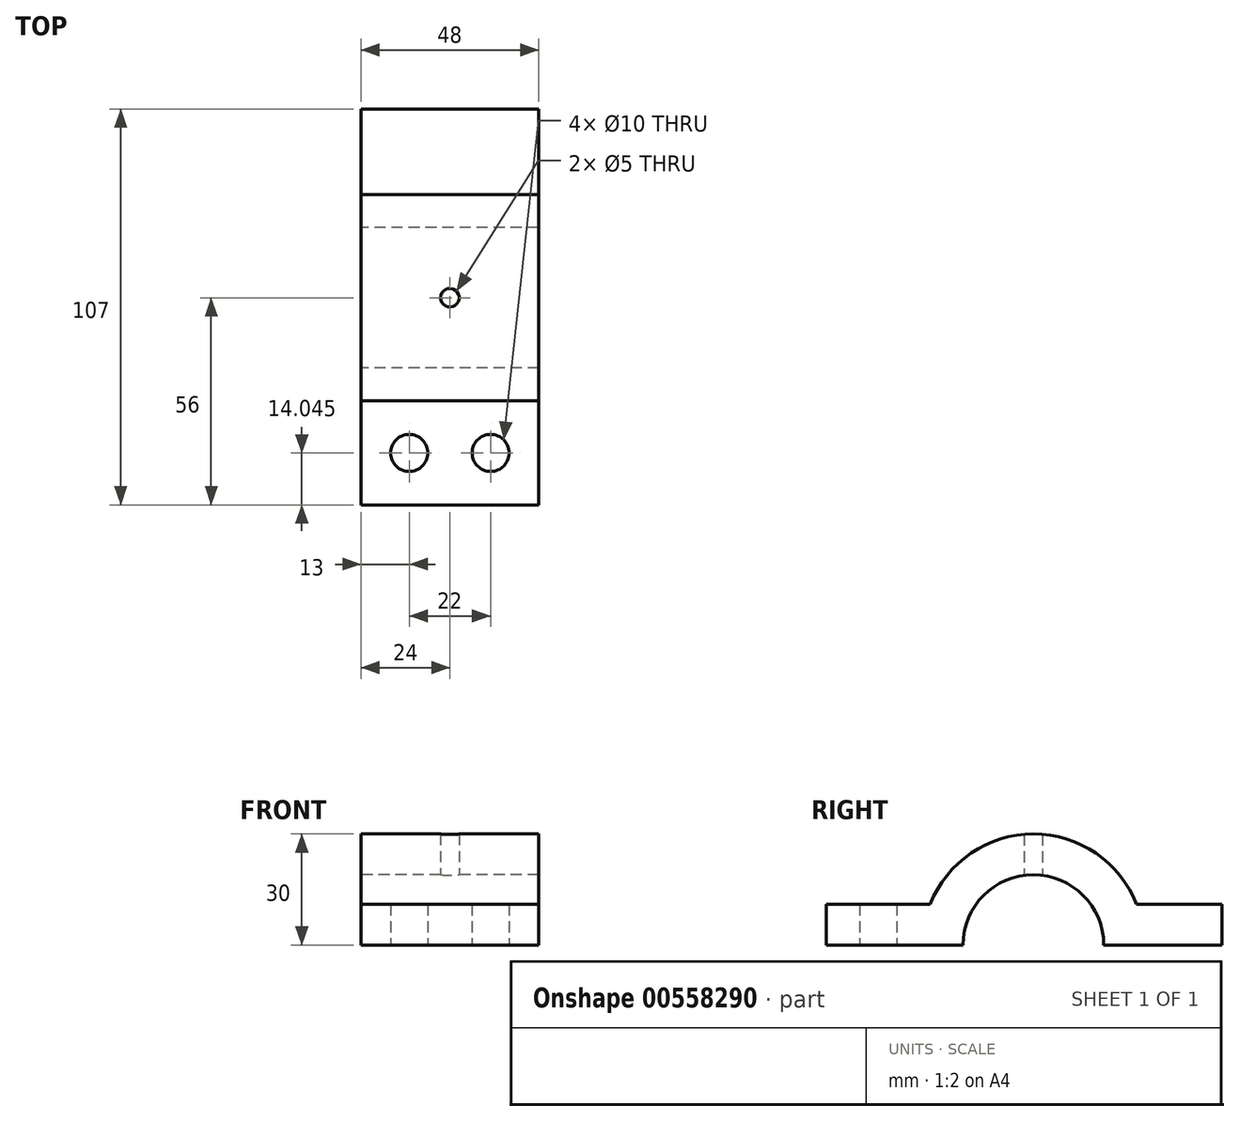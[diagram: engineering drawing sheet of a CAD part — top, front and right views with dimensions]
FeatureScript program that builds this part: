
annotation { "Feature Type Name" : "Feature", "Feature Type Description" : "" }
export const myFeature = defineFeature(function(context is Context, id is Id, definition is map)
    precondition{}
    {
        {
            var Q0;
            Q0=qCreatedBy(makeId("Right.planeOp"),FACE);
            var sketch = newSketch(context, id + "F0", { "sketchPlane" : qUnion([Q0])});
            skCircle(sketch, "E0", {"center": v(0, 0) * mm, "radius": 30 * mm});
            skCircle(sketch, "E1", {"center": v(0, 0) * mm, "radius": 19 * mm});
            skLineSegment(sketch, "E2.bottom", {"start": v(-56, 0) * mm, "end": v(51, 0) * mm});
            skLineSegment(sketch, "E2.top", {"start": v(-56, 11) * mm, "end": v(51, 11) * mm});
            skLineSegment(sketch, "E2.left", {"start": v(-56, 0) * mm, "end": v(-56, 11) * mm});
            skLineSegment(sketch, "E2.right", {"start": v(51, 0) * mm, "end": v(51, 11) * mm});
            skLineSegment(sketch, "E3.bottom", {"start": v(51, 11) * mm, "end": v(40, 11) * mm});
            skLineSegment(sketch, "E3.top", {"start": v(51, 41) * mm, "end": v(40, 41) * mm});
            skLineSegment(sketch, "E3.left", {"start": v(51, 11) * mm, "end": v(51, 41) * mm});
            skLineSegment(sketch, "E3.right", {"start": v(40, 11) * mm, "end": v(40, 41) * mm});
            skSolve(sketch);
        }
        {
            var Q0;
            {var subQ5=sQuery(id+"F0.wireOp",EDGE,"E2.left");Q0=makeQuery(id+"F0.imprint","IMPRINT",FACE,{"disambiguationData":[TD([[makeQuery(id+"F0.imprint","IMPRINT",EDGE,{"derivedFrom":subQ5}),-1.0]])]});}
            var Q1;
            {var subQ0=sQuery(id+"F0.wireOp",EDGE,"E2.top");var subQ1=sQuery(id+"F0.wireOp",EDGE,"E0");var subQ2=makeQuery(id+"F0.imprint","INTERSECT",VERTEX,{"disambiguationData":[OD(1.0)],"derivedFrom":[subQ1,subQ0]});Q1=makeQuery(id+"F0.imprint","IMPRINT",FACE,{"disambiguationData":[TD([[makeQuery(id+"F0.imprint","IMPRINT",EDGE,{"disambiguationData":[TD([[subQ2,-1.0]])],"derivedFrom":subQ1}),1.0]])]});}
            var Q2;
            {var subQ0=sQuery(id+"F0.wireOp",EDGE,"E2.top");var subQ1=sQuery(id+"F0.wireOp",EDGE,"E0");var subQ2=makeQuery(id+"F0.imprint","INTERSECT",VERTEX,{"disambiguationData":[OD(0.0)],"derivedFrom":[subQ1,subQ0]});Q2=makeQuery(id+"F0.imprint","IMPRINT",FACE,{"disambiguationData":[TD([[makeQuery(id+"F0.imprint","IMPRINT",EDGE,{"disambiguationData":[TD([[subQ2,-1.0]])],"derivedFrom":subQ1}),1.0]])]});}
            var Q3;
            {var subQ0=sQuery(id+"F0.wireOp",EDGE,"E2.top");var subQ1=sQuery(id+"F0.wireOp",EDGE,"E0");var subQ2=makeQuery(id+"F0.imprint","INTERSECT",VERTEX,{"disambiguationData":[OD(0.0)],"derivedFrom":[subQ1,subQ0]});Q3=makeQuery(id+"F0.imprint","IMPRINT",FACE,{"disambiguationData":[TD([[makeQuery(id+"F0.imprint","IMPRINT",EDGE,{"disambiguationData":[TD([[subQ2,1.0]])],"derivedFrom":subQ1}),1.0]])]});}
            var Q4;
            {var subQ0=sQuery(id+"F0.wireOp",EDGE,"E2.right");Q4=makeQuery(id+"F0.imprint","IMPRINT",FACE,{"disambiguationData":[TD([[makeQuery(id+"F0.imprint","IMPRINT",EDGE,{"derivedFrom":subQ0}),1.0]])]});}
            var Q5;
            Q5=makeQuery(id+"F0.imprint","IMPRINT",FACE,{"disambiguationData":[TD([[makeQuery(id+"F0.imprint","IMPRINT",EDGE,{"derivedFrom":sQuery(id+"F0.wireOp",EDGE,"E3.bottom")}),-1.0]])]});
            extrude(context, id + "F1", {"entities" : qUnion([Q0, Q1, Q2, Q3, Q4, Q5]), "depth" : 48 * mm, "offsetDistance" : 25 * mm, "symmetric" : true});
        }
        {
            var Q0;
            Q0=makeQuery(id+"F1.opExtrude","SWEPT_FACE",FACE,{"disambiguationData":[OSD([sQuery(id+"F0.wireOp",EDGE,"E2.right"),sQuery(id+"F0.wireOp",EDGE,"E3.left")])]});
            var sketch = newSketch(context, id + "F2", { "sketchPlane" : qUnion([Q0])});
            skLineSegment(sketch, "E4", {"start": v(0, 41) * mm, "end": v(0, 0) * mm, "construction": true});
            skCircle(sketch, "E5", {"center": v(0, 25) * mm, "radius": 6.5 * mm});
            skLineSegment(sketch, "E6", {"start": v(-6.5, 25) * mm, "end": v(-6.5, 41) * mm});
            skLineSegment(sketch, "E7", {"start": v(6.5, 25) * mm, "end": v(6.5, 41) * mm});
            skLineSegment(sketch, "E8", {"start": v(-6.5, 41) * mm, "end": v(6.5, 41) * mm});
            skSolve(sketch);
        }
        {
            var Q0;
            {var subQ0=sQuery(id+"F2.wireOp",EDGE,"E6");Q0=makeQuery(id+"F2.imprint","IMPRINT",FACE,{"disambiguationData":[TD([[makeQuery(id+"F2.imprint","IMPRINT",EDGE,{"derivedFrom":subQ0}),-1.0]])]});}
            var Q1;
            {var subQ0=sQuery(id+"F2.wireOp",EDGE,"E5");var subQ3=makeQuery(id+"F2.imprint","IMPRINT",VERTEX,{"derivedFrom":subQ0});Q1=makeQuery(id+"F2.imprint","IMPRINT",FACE,{"disambiguationData":[TD([[makeQuery(id+"F2.imprint","IMPRINT",EDGE,{"disambiguationData":[TD([[subQ3,1.0]])],"derivedFrom":subQ0}),1.0]])]});}
            extrude(context, id + "F3", {"entities" : qUnion([Q0, Q1]), "operationType" : NewBodyOperationType.REMOVE, "oppositeDirection" : true, "depth" : 35.8 * mm, "offsetDistance" : 25 * mm, "symmetric" : true});
        }
        {
            var Q0;
            Q0=qCreatedBy(makeId("Top.planeOp"),FACE);
            var sketch = newSketch(context, id + "F4", { "sketchPlane" : qUnion([Q0])});
            skLineSegment(sketch, "E9", {"start": v(-24.17, -41.96) * mm, "end": v(-23.83, -41.96) * mm, "construction": true});
            skLineSegment(sketch, "E10", {"start": v(-23.83, -41.96) * mm, "end": v(24.07, -41.96) * mm, "construction": true});
            skLineSegment(sketch, "E11", {"start": v(0, -56.1) * mm, "end": v(0, -28.03) * mm, "construction": true});
            skCircle(sketch, "E12", {"center": v(0, 0) * mm, "radius": 2.5 * mm});
            skCircle(sketch, "E13", {"center": v(-11, -41.96) * mm, "radius": 5 * mm});
            skCircle(sketch, "E14", {"center": v(11, -41.96) * mm, "radius": 5 * mm});
            skSolve(sketch);
        }
        {
            var Q0;
            Q0=makeQuery(id+"F4.imprint","IMPRINT",FACE,{"disambiguationData":[TD([[makeQuery(id+"F4.imprint","IMPRINT",EDGE,{"derivedFrom":sQuery(id+"F4.wireOp",EDGE,"E13")}),1.0]])]});
            var Q1;
            Q1=makeQuery(id+"F4.imprint","IMPRINT",FACE,{"disambiguationData":[TD([[makeQuery(id+"F4.imprint","IMPRINT",EDGE,{"derivedFrom":sQuery(id+"F4.wireOp",EDGE,"E14")}),1.0]])]});
            var Q2;
            Q2=makeQuery(id+"F4.imprint","IMPRINT",FACE,{"disambiguationData":[TD([[makeQuery(id+"F4.imprint","IMPRINT",EDGE,{"derivedFrom":sQuery(id+"F4.wireOp",EDGE,"E12")}),1.0]])]});
            extrude(context, id + "F5", {"entities" : qUnion([Q0, Q1, Q2]), "operationType" : NewBodyOperationType.REMOVE, "depth" : 102.4 * mm, "offsetDistance" : 25 * mm, "symmetric" : true});
        }
    });
